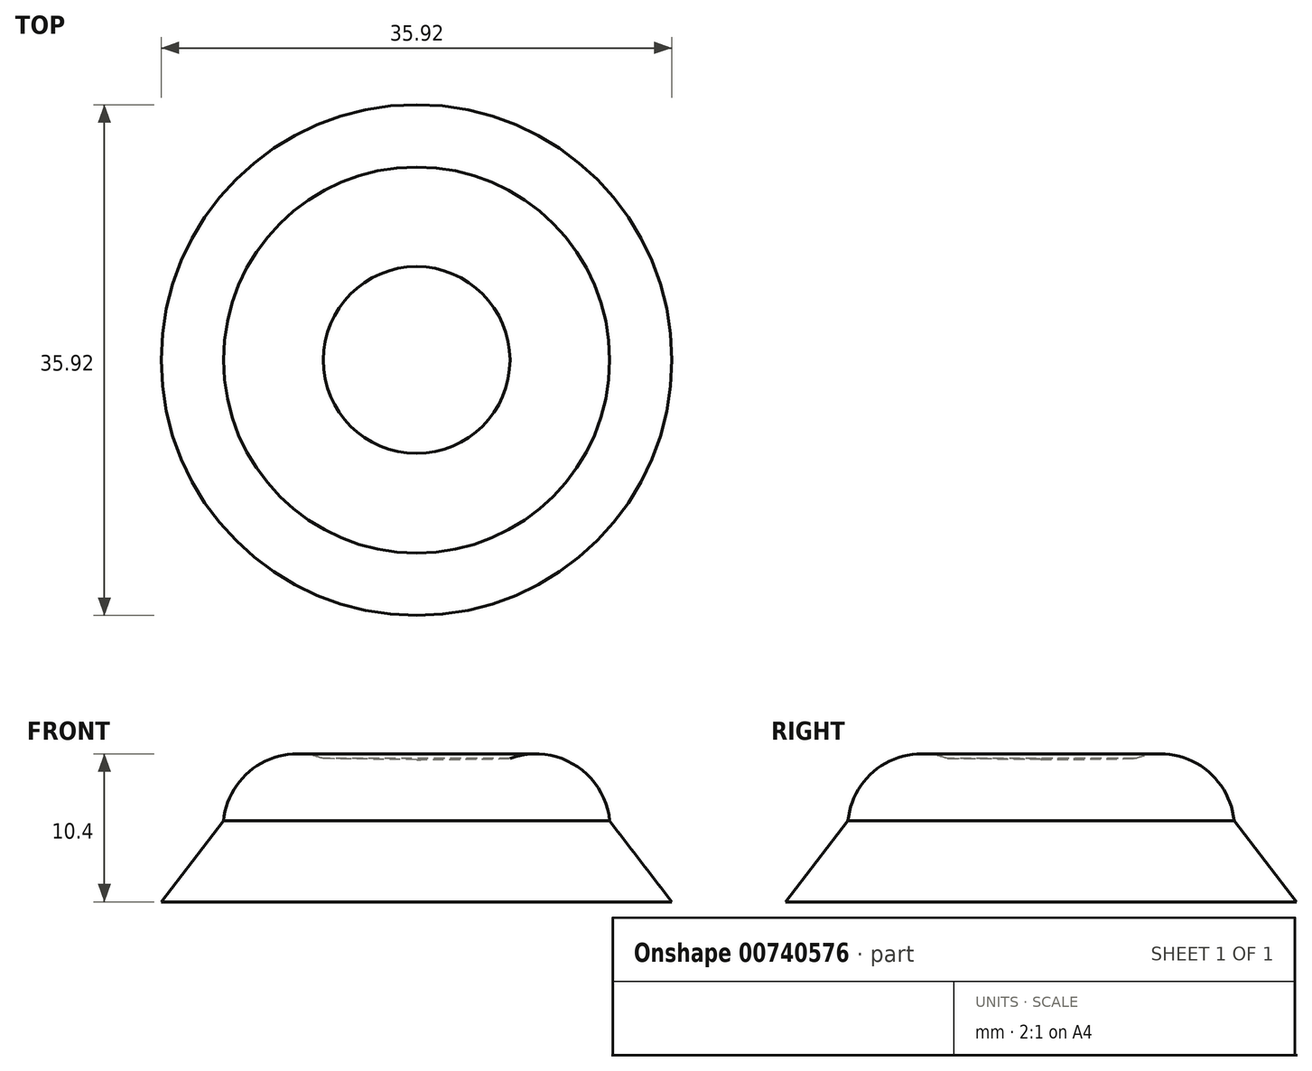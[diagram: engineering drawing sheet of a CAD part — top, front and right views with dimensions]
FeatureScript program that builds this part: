
annotation { "Feature Type Name" : "Feature", "Feature Type Description" : "" }
export const myFeature = defineFeature(function(context is Context, id is Id, definition is map)
    precondition{}
    {
        {
            var Q0;
            Q0=qCreatedBy(makeId("Front.planeOp"),FACE);
            var sketch = newSketch(context, id + "F0", { "sketchPlane" : qUnion([Q0])});
            skLineSegment(sketch, "E0", {"start": v(0, 10) * mm, "end": v(0, 0) * mm});
            skArc(sketch, "E1", {"start": v(13.58, 5.7) * mm, "mid": v(11.16, 9.61) * mm, "end": v(6.57, 10.08) * mm});
            skPoint(sketch, "E2.orphan", {"position": v(7.89, 0) * mm});
            skLineSegment(sketch, "E3", {"start": v(7.89, 0) * mm, "end": v(17.96, 0) * mm});
            skLineSegment(sketch, "E4", {"start": v(17.96, 0) * mm, "end": v(13.58, 5.7) * mm});
            skLineSegment(sketch, "E5", {"start": v(6.57, 10.08) * mm, "end": v(0, 10) * mm});
            skLineSegment(sketch, "E6", {"start": v(7.89, 0) * mm, "end": v(0, 0) * mm});
            skSolve(sketch);
        }
        {
            var Q0;
            Q0=makeQuery(id+"F0.imprint","IMPRINT",FACE,{"disambiguationData":[TD([[makeQuery(id+"F0.imprint","IMPRINT",EDGE,{"derivedFrom":sQuery(id+"F0.wireOp",EDGE,"E1")}),1.0]])]});
            var Q1;
            Q1=sQuery(id+"F0.wireOp",EDGE,"E0");
            revolve(context, id + "F1", {"surfaceOperationType" : NewSurfaceOperationType.NEW, "entities" : qUnion([Q0]), "axis" : qUnion([Q1]), "revolveType" : RevolveType.FULL});
        }
    });
